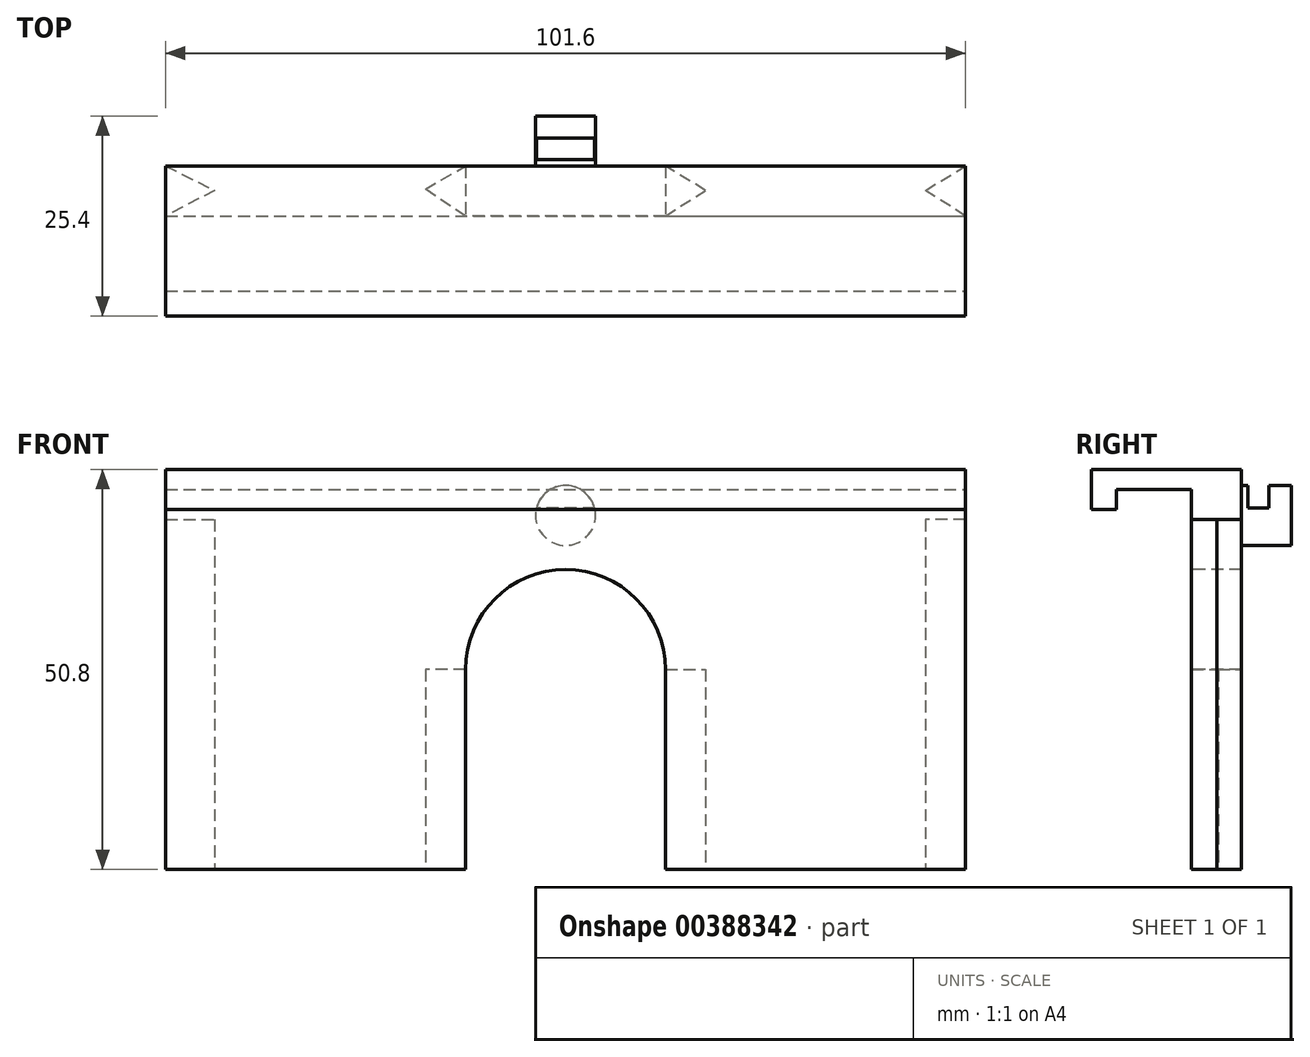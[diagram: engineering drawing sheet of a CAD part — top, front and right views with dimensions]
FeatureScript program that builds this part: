
annotation { "Feature Type Name" : "Feature", "Feature Type Description" : "" }
export const myFeature = defineFeature(function(context is Context, id is Id, definition is map)
    precondition{}
    {
        {
            var Q0;
            Q0=qCreatedBy(makeId("Front.planeOp"),FACE);
            var sketch = newSketch(context, id + "F0", { "sketchPlane" : qUnion([Q0])});
            skLineSegment(sketch, "E0.bottom", {"start": v(0, 0) * mm, "end": v(101.6, 0) * mm});
            skLineSegment(sketch, "E0.top", {"start": v(0, 50.8) * mm, "end": v(101.6, 50.8) * mm});
            skLineSegment(sketch, "E0.left", {"start": v(0, 0) * mm, "end": v(0, 50.8) * mm});
            skLineSegment(sketch, "E0.right", {"start": v(101.6, 0) * mm, "end": v(101.6, 50.8) * mm});
            skSolve(sketch);
        }
        {
            var Q0;
            Q0=qSketchRegion(id+"F0",true);
            extrude(context, id + "F1", {"entities" : qUnion([Q0]), "depth" : 6.35 * mm});
        }
        {
            var Q0;
            Q0=makeQuery(id+"F1.opExtrude","CAP_FACE",FACE,{"disambiguationData":[OSD([sQuery(id+"F0.wireOp",EDGE,"E0.bottom"),sQuery(id+"F0.wireOp",EDGE,"E0.top"),sQuery(id+"F0.wireOp",EDGE,"E0.left"),sQuery(id+"F0.wireOp",EDGE,"E0.right")])],"isStart":false});
            var sketch = newSketch(context, id + "F2", { "sketchPlane" : qUnion([Q0])});
            skLineSegment(sketch, "E1.bottom", {"start": v(0, 50.8) * mm, "end": v(101.6, 50.8) * mm});
            skLineSegment(sketch, "E1.top", {"start": v(0, 45.72) * mm, "end": v(101.6, 45.72) * mm});
            skLineSegment(sketch, "E1.left", {"start": v(0, 50.8) * mm, "end": v(0, 45.72) * mm});
            skLineSegment(sketch, "E1.right", {"start": v(101.6, 50.8) * mm, "end": v(101.6, 45.72) * mm});
            skSolve(sketch);
        }
        {
            var Q0;
            Q0=qSketchRegion(id+"F2",true);
            extrude(context, id + "F3", {"entities" : qUnion([Q0]), "operationType" : NewBodyOperationType.ADD, "depth" : 12.7 * mm});
        }
        {
            var Q0;
            Q0=makeQuery(id+"F3.boolean.opBoolean","MERGE",FACE,{"derivedFrom":[makeQuery(id+"F1.opExtrude","SWEPT_FACE",FACE,{"disambiguationData":[OSD([sQuery(id+"F0.wireOp",EDGE,"E0.right")])]}),makeQuery(id+"F3.opExtrude","SWEPT_FACE",FACE,{"disambiguationData":[OSD([sQuery(id+"F2.wireOp",EDGE,"E1.right")])]})]});
            var sketch = newSketch(context, id + "F4", { "sketchPlane" : qUnion([Q0])});
            skLineSegment(sketch, "E2.bottom", {"start": v(-15.88, 45.72) * mm, "end": v(-6.35, 45.72) * mm});
            skLineSegment(sketch, "E2.top", {"start": v(-15.88, 48.26) * mm, "end": v(-6.35, 48.26) * mm});
            skLineSegment(sketch, "E2.left", {"start": v(-15.88, 45.72) * mm, "end": v(-15.88, 48.26) * mm});
            skLineSegment(sketch, "E2.right", {"start": v(-6.35, 45.72) * mm, "end": v(-6.35, 48.26) * mm});
            skSolve(sketch);
        }
        {
            var Q0;
            Q0=makeQuery(id+"F4.imprint","IMPRINT",FACE,{"disambiguationData":[TD([[makeQuery(id+"F4.imprint","IMPRINT",EDGE,{"derivedFrom":sQuery(id+"F4.wireOp",EDGE,"E2.bottom")}),1.0]])]});
            extrude(context, id + "F5", {"entities" : qUnion([Q0]), "operationType" : NewBodyOperationType.REMOVE, "oppositeDirection" : true, "depth" : 127.3 * mm});
        }
        {
            var Q0;
            Q0=makeQuery(id+"F5.boolean.opBoolean","MERGE",FACE,{"derivedFrom":[makeQuery(id+"F1.opExtrude","CAP_FACE",FACE,{"disambiguationData":[OSD([sQuery(id+"F0.wireOp",EDGE,"E0.bottom"),sQuery(id+"F0.wireOp",EDGE,"E0.top"),sQuery(id+"F0.wireOp",EDGE,"E0.left"),sQuery(id+"F0.wireOp",EDGE,"E0.right")])],"isStart":false}),makeQuery(id+"F5.opExtrude","SWEPT_FACE",FACE,{"disambiguationData":[OSD([sQuery(id+"F4.wireOp",EDGE,"E2.right")])]})]});
            var sketch = newSketch(context, id + "F6", { "sketchPlane" : qUnion([Q0])});
            skLineSegment(sketch, "E3.bottom", {"start": v(38.1, 0) * mm, "end": v(63.5, 0) * mm});
            skLineSegment(sketch, "E3.left", {"start": v(38.1, 0) * mm, "end": v(38.1, 25.4) * mm});
            skLineSegment(sketch, "E3.right", {"start": v(63.5, 0) * mm, "end": v(63.5, 25.4) * mm});
            skArc(sketch, "E4", {"start": v(63.5, 25.4) * mm, "mid": v(50.8, 38.1) * mm, "end": v(38.1, 25.4) * mm});
            skPoint(sketch, "E5.orphan", {"position": v(50.8, 0) * mm});
            skSolve(sketch);
        }
        {
            var Q0;
            Q0=qSketchRegion(id+"F6",true);
            extrude(context, id + "F7", {"entities" : qUnion([Q0]), "operationType" : NewBodyOperationType.REMOVE, "oppositeDirection" : true, "depth" : 25.4 * mm});
        }
        {
            var Q0;
            {var subQ0=sQuery(id+"F0.wireOp",EDGE,"E0.right");var subQ3=sQuery(id+"F0.wireOp",EDGE,"E0.bottom");Q0=makeQuery(id+"F7.boolean.opBoolean","SPLIT",FACE,{"disambiguationData":[TD([makeQuery(id+"F1.opExtrude","SWEPT_FACE",FACE,{"disambiguationData":[OSD([subQ0])]})])],"derivedFrom":makeQuery(id+"F1.opExtrude","SWEPT_FACE",FACE,{"disambiguationData":[OSD([subQ3])]})});}
            var sketch = newSketch(context, id + "F8", { "sketchPlane" : qUnion([Q0])});
            skPoint(sketch, "E6", {"position": v(68.58, 3.1) * mm});
            skPoint(sketch, "E7", {"position": v(33.02, 2.94) * mm});
            skPoint(sketch, "E8", {"position": v(38.1, 0) * mm});
            skPoint(sketch, "E9", {"position": v(63.5, 0) * mm});
            skPoint(sketch, "E10", {"position": v(63.5, 6.35) * mm});
            skPoint(sketch, "E11", {"position": v(38.1, 6.35) * mm});
            skLineSegment(sketch, "E12", {"start": v(33.02, 2.94) * mm, "end": v(38.1, 0) * mm});
            skLineSegment(sketch, "E13", {"start": v(38.1, 6.35) * mm, "end": v(33.02, 2.94) * mm});
            skLineSegment(sketch, "E14", {"start": v(63.5, 6.35) * mm, "end": v(68.58, 3.1) * mm});
            skLineSegment(sketch, "E15", {"start": v(68.58, 3.1) * mm, "end": v(68.58, 3.1) * mm});
            skLineSegment(sketch, "E16", {"start": v(68.58, 3.1) * mm, "end": v(63.5, 0) * mm});
            skLineSegment(sketch, "E17", {"start": v(38.1, 0) * mm, "end": v(38.1, 6.35) * mm});
            skLineSegment(sketch, "E18", {"start": v(63.5, 0) * mm, "end": v(63.5, 6.35) * mm});
            skSolve(sketch);
        }
        {
            var Q0;
            Q0=qSketchRegion(id+"F8",true);
            extrude(context, id + "F9", {"entities" : qUnion([Q0]), "operationType" : NewBodyOperationType.REMOVE, "oppositeDirection" : true, "depth" : 25.4 * mm});
        }
        {
            var Q0;
            {var subQ0=sQuery(id+"F0.wireOp",EDGE,"E0.right");var subQ3=sQuery(id+"F0.wireOp",EDGE,"E0.bottom");Q0=makeQuery(id+"F7.boolean.opBoolean","SPLIT",FACE,{"disambiguationData":[TD([makeQuery(id+"F1.opExtrude","SWEPT_FACE",FACE,{"disambiguationData":[OSD([subQ0])]})])],"derivedFrom":makeQuery(id+"F1.opExtrude","SWEPT_FACE",FACE,{"disambiguationData":[OSD([subQ3])]})});}
            var sketch = newSketch(context, id + "F10", { "sketchPlane" : qUnion([Q0])});
            skPoint(sketch, "E19", {"position": v(96.52, 3.1) * mm});
            skLineSegment(sketch, "E20", {"start": v(96.52, 3.1) * mm, "end": v(101.6, 0) * mm});
            skLineSegment(sketch, "E21", {"start": v(101.6, 0) * mm, "end": v(101.6, 6.35) * mm});
            skLineSegment(sketch, "E22", {"start": v(101.6, 6.35) * mm, "end": v(96.52, 3.1) * mm});
            skPoint(sketch, "E23", {"position": v(6.22, 3.1) * mm});
            skPoint(sketch, "E24", {"position": v(0, 6.35) * mm});
            skLineSegment(sketch, "E25", {"start": v(0, 0) * mm, "end": v(6.22, 3.1) * mm});
            skLineSegment(sketch, "E26", {"start": v(6.22, 3.1) * mm, "end": v(6.22, 3.1) * mm});
            skLineSegment(sketch, "E27", {"start": v(6.22, 3.1) * mm, "end": v(0, 6.35) * mm});
            skLineSegment(sketch, "E28", {"start": v(0, 6.35) * mm, "end": v(0, 6.35) * mm});
            skLineSegment(sketch, "E29", {"start": v(0, 0) * mm, "end": v(0, 6.35) * mm});
            skSolve(sketch);
        }
        {
            var Q0;
            Q0 = qSketchRegion(id + "F10", true);
            extrude(context, id + "F11", {"entities" : qUnion([Q0]), "operationType" : NewBodyOperationType.REMOVE, "oppositeDirection" : true, "depth" : 44.45 * mm});
        }
        {
            var Q0;
            Q0=makeQuery(id+"F1.opExtrude","CAP_FACE",FACE,{"disambiguationData":[OSD([sQuery(id+"F0.wireOp",EDGE,"E0.bottom"),sQuery(id+"F0.wireOp",EDGE,"E0.top"),sQuery(id+"F0.wireOp",EDGE,"E0.left"),sQuery(id+"F0.wireOp",EDGE,"E0.right")])],"isStart":true});
            var sketch = newSketch(context, id + "F12", { "sketchPlane" : qUnion([Q0])});
            skCircle(sketch, "E30", {"center": v(-50.8, 44.97) * mm, "radius": 3.81 * mm});
            skPoint(sketch, "E30.centerSnap0", {"position": v(-50.8, 50.8) * mm});
            skSolve(sketch);
        }
        {
            var Q0;
            Q0 = qSketchRegion(id + "F12", true);
            var Q1;
            Q1=makeQuery(id+"F12.imprint","IMPRINT",FACE,{"disambiguationData":[TD([[makeQuery(id+"F12.imprint","IMPRINT",EDGE,{"derivedFrom":sQuery(id+"F12.wireOp",EDGE,"E30")}),1.0]])]});
            extrude(context, id + "F13", {"entities" : qUnion([Q0, Q1]), "operationType" : NewBodyOperationType.ADD, "depth" : 6.35 * mm});
        }
        {
            var Q0;
            Q0=qCreatedBy(makeId("Right.planeOp"),FACE);
            var sketch = newSketch(context, id + "F14", { "sketchPlane" : qUnion([Q0])});
            skLineSegment(sketch, "E31.bottom", {"start": v(0.86, 49) * mm, "end": v(3.53, 49) * mm});
            skLineSegment(sketch, "E31.top", {"start": v(0.86, 45.9) * mm, "end": v(3.53, 45.9) * mm});
            skLineSegment(sketch, "E31.left", {"start": v(0.86, 49) * mm, "end": v(0.86, 45.9) * mm});
            skLineSegment(sketch, "E31.right", {"start": v(3.53, 49) * mm, "end": v(3.53, 45.9) * mm});
            skSolve(sketch);
        }
        {
            var Q0;
            Q0=makeQuery(id+"F14.imprint","IMPRINT",FACE,{"disambiguationData":[TD([[makeQuery(id+"F14.imprint","IMPRINT",EDGE,{"derivedFrom":sQuery(id+"F14.wireOp",EDGE,"E31.bottom")}),-1.0]])]});
            extrude(context, id + "F15", {"entities" : qUnion([Q0]), "operationType" : NewBodyOperationType.REMOVE, "depth" : 113.54 * mm});
        }
    });
